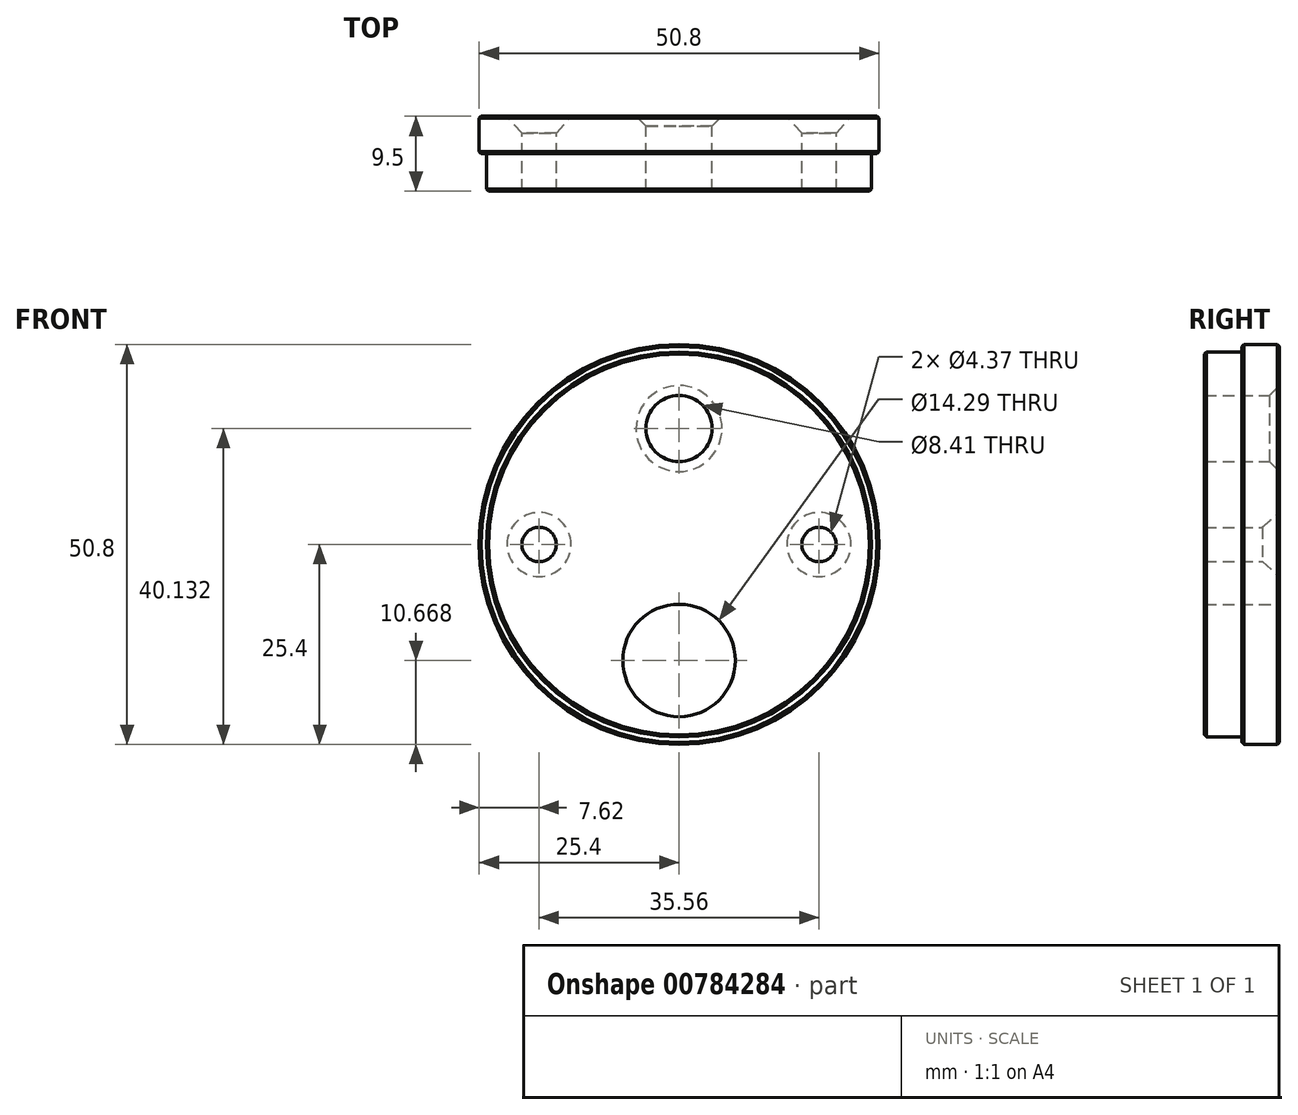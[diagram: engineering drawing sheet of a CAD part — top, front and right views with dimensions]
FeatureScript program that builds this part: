
annotation { "Feature Type Name" : "Feature", "Feature Type Description" : "" }
export const myFeature = defineFeature(function(context is Context, id is Id, definition is map)
    precondition{}
    {
        {
            var Q0;
            Q0=qCreatedBy(makeId("Right.planeOp"),FACE);
            var sketch = newSketch(context, id + "F0", { "sketchPlane" : qUnion([Q0])});
            skLineSegment(sketch, "E0", {"start": v(0, 24.45) * mm, "end": v(4.75, 24.45) * mm});
            skLineSegment(sketch, "E1", {"start": v(4.75, 24.45) * mm, "end": v(4.75, 25.4) * mm});
            skLineSegment(sketch, "E2", {"start": v(4.75, 25.4) * mm, "end": v(9.5, 25.4) * mm});
            skLineSegment(sketch, "E3", {"start": v(9.5, 25.4) * mm, "end": v(9.5, 0) * mm});
            skLineSegment(sketch, "E4", {"start": v(0, 0) * mm, "end": v(0, 24.45) * mm});
            skLineSegment(sketch, "E5", {"start": v(0, 0) * mm, "end": v(10.24, 0) * mm, "construction": true});
            skLineSegment(sketch, "E6", {"start": v(9.5, 0) * mm, "end": v(0, 0) * mm});
            skSolve(sketch);
        }
        {
            var Q0;
            Q0 = qSketchRegion(id + "F0", true);
            var Q1;
            Q1=sQuery(id+"F0.wireOp",EDGE,"E5");
            revolve(context, id + "F1", {"surfaceOperationType" : NewSurfaceOperationType.NEW, "entities" : qUnion([Q0]), "axis" : qUnion([Q1]), "revolveType" : RevolveType.FULL});
        }
        {
            var Q0;
            Q0=makeQuery(id+"F1.opRevolve","SWEPT_FACE",FACE,{"disambiguationData":[OSD([sQuery(id+"F0.wireOp",EDGE,"E3")])]});
            var sketch = newSketch(context, id + "F2", { "sketchPlane" : qUnion([Q0])});
            skPoint(sketch, "E7", {"position": v(0, -14.73) * mm});
            skPoint(sketch, "E8", {"position": v(0, 14.73) * mm});
            skPoint(sketch, "E9", {"position": v(-17.78, 0) * mm});
            skPoint(sketch, "E10", {"position": v(17.78, 0) * mm});
            skCircle(sketch, "E11", {"center": v(0, 0) * mm, "radius": 17.78 * mm, "construction": true});
            skSolve(sketch);
        }
        {
            var Q0;
            Q0=sQuery(id+"F2.wireOp",VERTEX,"E7");
            var Q1;
            Q1=makeQuery(id+"F1.opRevolve","SWEPT_BODY",BODY,{"disambiguationData":[OSD([sQuery(id+"F0.wireOp",EDGE,"E0"),sQuery(id+"F0.wireOp",EDGE,"E1"),sQuery(id+"F0.wireOp",EDGE,"E2"),sQuery(id+"F0.wireOp",EDGE,"E3"),sQuery(id+"F0.wireOp",EDGE,"0isxcHgc-XUNQ-irVL-t00k-W9mPTENeI8QK"),sQuery(id+"F0.wireOp",EDGE,"wkJbMm6k-2pAR-Olap-LmwG-vrIJT3S7KMNY"),sQuery(id+"F0.wireOp",EDGE,"E4")])]});
            hole(context, id + "F3", {"style" : HoleStyle.SIMPLE, "endStyle" : HoleEndStyle.THROUGH, "holeDiameter" : 14.29 * mm, "majorDiameter" : 6.35 * mm, "isTappedThrough" : true, "tappedDepth" : 12.7 * mm, "tapClearance" : 3, "startFromSketch" : true, "locations" : qUnion([Q0]), "scope" : qUnion([Q1])});
        }
        {
            var Q0;
            Q0=sQuery(id+"F2.wireOp",VERTEX,"E8");
            var Q1;
            Q1=makeQuery(id+"F1.opRevolve","SWEPT_BODY",BODY,{"disambiguationData":[OSD([sQuery(id+"F0.wireOp",EDGE,"E0"),sQuery(id+"F0.wireOp",EDGE,"E1"),sQuery(id+"F0.wireOp",EDGE,"E2"),sQuery(id+"F0.wireOp",EDGE,"E3"),sQuery(id+"F0.wireOp",EDGE,"0isxcHgc-XUNQ-irVL-t00k-W9mPTENeI8QK"),sQuery(id+"F0.wireOp",EDGE,"wkJbMm6k-2pAR-Olap-LmwG-vrIJT3S7KMNY"),sQuery(id+"F0.wireOp",EDGE,"E4")])]});
            hole(context, id + "F4", {"style" : HoleStyle.C_SINK, "endStyle" : HoleEndStyle.THROUGH, "holeDiameter" : 8.4 * mm, "cSinkDiameter" : 10.92 * mm, "cSinkAngle" : 90 * degree, "majorDiameter" : 6.35 * mm, "isTappedThrough" : true, "tappedDepth" : 12.7 * mm, "tapClearance" : 3, "startFromSketch" : true, "locations" : qUnion([Q0]), "scope" : qUnion([Q1])});
        }
        {
            var Q0;
            Q0=sQuery(id+"F2.wireOp",VERTEX,"E9");
            var Q1;
            Q1=sQuery(id+"F2.wireOp",VERTEX,"E10");
            var Q2;
            Q2=makeQuery(id+"F1.opRevolve","SWEPT_BODY",BODY,{"disambiguationData":[OSD([sQuery(id+"F0.wireOp",EDGE,"E0"),sQuery(id+"F0.wireOp",EDGE,"E1"),sQuery(id+"F0.wireOp",EDGE,"E2"),sQuery(id+"F0.wireOp",EDGE,"E3"),sQuery(id+"F0.wireOp",EDGE,"0isxcHgc-XUNQ-irVL-t00k-W9mPTENeI8QK"),sQuery(id+"F0.wireOp",EDGE,"wkJbMm6k-2pAR-Olap-LmwG-vrIJT3S7KMNY"),sQuery(id+"F0.wireOp",EDGE,"E4")])]});
            hole(context, id + "F5", {"style" : HoleStyle.C_SINK, "endStyle" : HoleEndStyle.THROUGH, "holeDiameter" : 4.37 * mm, "cSinkDiameter" : 8.13 * mm, "cSinkAngle" : 82 * degree, "majorDiameter" : 4.17 * mm, "isTappedThrough" : true, "tappedDepth" : 12.7 * mm, "tapClearance" : 3, "startFromSketch" : true, "locations" : qUnion([Q0, Q1]), "scope" : qUnion([Q2])});
        }
        {
            var Q0;
            Q0=makeQuery(id+"F1.opRevolve","SWEPT_EDGE",EDGE,{"disambiguationData":[OSD([sQuery(id+"F0.wireOp",EDGE,"E2"),sQuery(id+"F0.wireOp",EDGE,"E3")])]});
            var Q1;
            Q1=makeQuery(id+"F3.hole-0.boolean.opBoolean","COPY",FACE,{"derivedFrom":makeQuery(id+"F3.hole-0.opRevolve","SWEPT_FACE",FACE,{"disambiguationData":[OSD([sQuery(id+"F3.hole-0.sketch.wireOp",EDGE,"core_line_2")])]})});
            var Q2;
            Q2=makeQuery(id+"F1.opRevolve","SWEPT_EDGE",EDGE,{"disambiguationData":[OSD([sQuery(id+"F0.wireOp",EDGE,"E0"),sQuery(id+"F0.wireOp",EDGE,"E4")])]});
            var Q3;
            Q3=makeQuery(id+"F4.hole-0.boolean.opBoolean","INTERSECT",EDGE,{"derivedFrom":[makeQuery(id+"F1.opRevolve","SWEPT_FACE",FACE,{"disambiguationData":[OSD([sQuery(id+"F0.wireOp",EDGE,"E4")])]}),makeQuery(id+"F4.hole-0.opRevolve","SWEPT_FACE",FACE,{"disambiguationData":[OSD([sQuery(id+"F4.hole-0.sketch.wireOp",EDGE,"core_line_2")])]})]});
            var Q4;
            Q4=makeQuery(id+"F1.opRevolve","SWEPT_EDGE",EDGE,{"disambiguationData":[OSD([sQuery(id+"F0.wireOp",EDGE,"E1"),sQuery(id+"F0.wireOp",EDGE,"E2")])]});
            chamfer(context, id + "F6", {"entities" : qUnion([Q0, Q1, Q2, Q3, Q4]), "chamferType" : ChamferType.OFFSET_ANGLE, "width" : 0.25 * mm, "oppositeDirection" : false, "angle" : 45 * degree, "tangentPropagation" : true});
        }
    });
